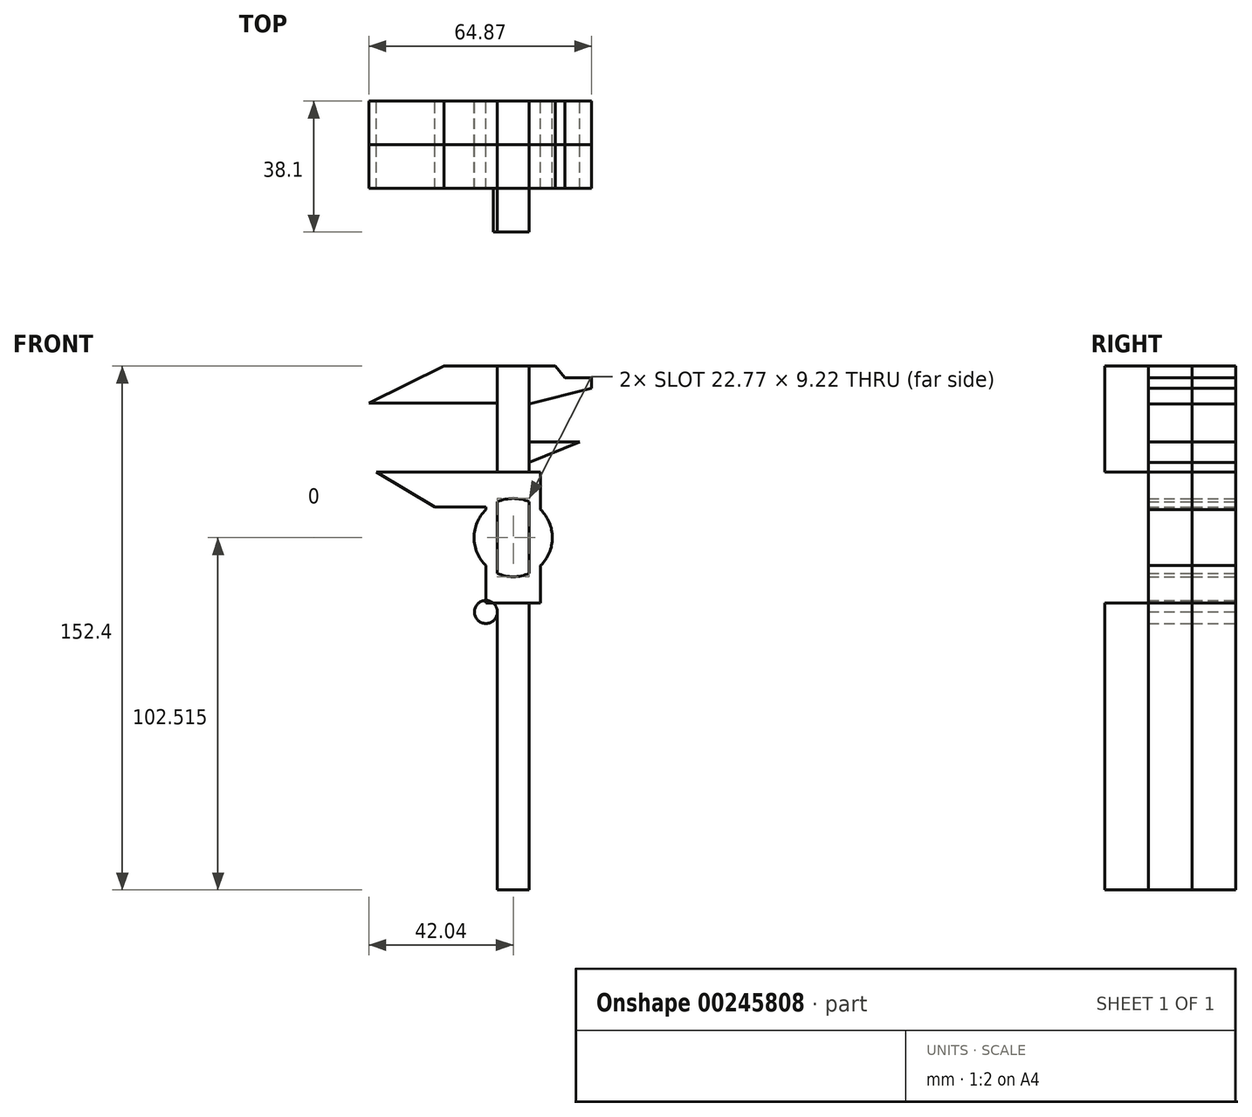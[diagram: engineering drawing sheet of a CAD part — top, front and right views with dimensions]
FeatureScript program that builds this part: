
annotation { "Feature Type Name" : "Feature", "Feature Type Description" : "" }
export const myFeature = defineFeature(function(context is Context, id is Id, definition is map)
    precondition{}
    {
        {
            var Q0;
            Q0=qCreatedBy(makeId("Front.planeOp"),FACE);
            var sketch = newSketch(context, id + "F0", { "sketchPlane" : qUnion([Q0])});
            skLineSegment(sketch, "E0.bottom", {"start": v(4.61, 76.2) * mm, "end": v(-4.61, 76.2) * mm});
            skLineSegment(sketch, "E0.top", {"start": v(4.61, -76.2) * mm, "end": v(-4.61, -76.2) * mm});
            skLineSegment(sketch, "E0.left", {"start": v(4.61, 76.2) * mm, "end": v(4.61, -76.2) * mm});
            skLineSegment(sketch, "E0.right", {"start": v(-4.61, 76.2) * mm, "end": v(-4.61, -76.2) * mm});
            skPoint(sketch, "E0.middle", {"position": v(0, 0) * mm});
            skLineSegment(sketch, "E1.bottom", {"start": v(7.97, 7.27) * mm, "end": v(-7.97, 7.27) * mm});
            skLineSegment(sketch, "E1.top", {"start": v(7.97, 45.37) * mm, "end": v(-7.97, 45.37) * mm});
            skLineSegment(sketch, "E1.left", {"start": v(7.97, 7.27) * mm, "end": v(7.97, 45.37) * mm});
            skLineSegment(sketch, "E1.right", {"start": v(-7.97, 7.27) * mm, "end": v(-7.97, 45.37) * mm});
            skPoint(sketch, "E1.middle", {"position": v(0, 26.32) * mm});
            skLineSegment(sketch, "E2", {"start": v(-4.61, 76.2) * mm, "end": v(-20.14, 76.2) * mm});
            skLineSegment(sketch, "E3", {"start": v(-20.14, 76.2) * mm, "end": v(-42.04, 65.5) * mm});
            skLineSegment(sketch, "E4", {"start": v(-42.04, 65.5) * mm, "end": v(-4.61, 65.5) * mm});
            skLineSegment(sketch, "E5", {"start": v(-7.97, 45.37) * mm, "end": v(-39.88, 45.37) * mm});
            skLineSegment(sketch, "E6", {"start": v(-39.88, 45.37) * mm, "end": v(-22.85, 35.24) * mm});
            skLineSegment(sketch, "E7", {"start": v(-22.85, 35.24) * mm, "end": v(-7.97, 35.24) * mm});
            skLineSegment(sketch, "E8", {"start": v(4.61, 76.2) * mm, "end": v(12.3, 76.2) * mm});
            skLineSegment(sketch, "E9", {"start": v(12.3, 76.2) * mm, "end": v(15, 72.8) * mm});
            skLineSegment(sketch, "E10", {"start": v(15, 72.8) * mm, "end": v(17.97, 72.8) * mm});
            skLineSegment(sketch, "E11", {"start": v(17.97, 72.8) * mm, "end": v(22.83, 72.8) * mm});
            skLineSegment(sketch, "E12", {"start": v(22.83, 72.8) * mm, "end": v(22.83, 69.83) * mm});
            skLineSegment(sketch, "E13", {"start": v(22.83, 69.83) * mm, "end": v(4.61, 65.24) * mm});
            skLineSegment(sketch, "E14", {"start": v(4.61, 54.16) * mm, "end": v(19.32, 54.16) * mm});
            skLineSegment(sketch, "E15", {"start": v(19.32, 54.16) * mm, "end": v(4.61, 48.2) * mm});
            skCircle(sketch, "E16", {"center": v(0, 26.32) * mm, "radius": 11.39 * mm});
            skCircle(sketch, "E17", {"center": v(-7.97, 4.7) * mm, "radius": 3.35 * mm});
            skSolve(sketch);
        }
        {
            var Q0;
            {var subQ0=sQuery(id+"F0.wireOp",EDGE,"E1.right");var subQ1=sQuery(id+"F0.wireOp",EDGE,"E1.bottom");var subQ2=makeQuery(id+"F0.imprint","INTERSECT",VERTEX,{"derivedFrom":[subQ1,subQ0]});Q0=makeQuery(id+"F0.imprint","IMPRINT",FACE,{"disambiguationData":[TD([[makeQuery(id+"F0.imprint","IMPRINT",EDGE,{"disambiguationData":[TD([[subQ2,1.0]])],"derivedFrom":subQ1}),-1.0]])]});}
            var Q1;
            {var subQ0=sQuery(id+"F0.wireOp",EDGE,"E17");var subQ1=sQuery(id+"F0.wireOp",EDGE,"E0.right");var subQ2=makeQuery(id+"F0.imprint","INTERSECT",VERTEX,{"derivedFrom":[subQ1,subQ0]});Q1=makeQuery(id+"F0.imprint","IMPRINT",FACE,{"disambiguationData":[TD([[makeQuery(id+"F0.imprint","IMPRINT",EDGE,{"disambiguationData":[TD([[subQ2,1.0]])],"derivedFrom":subQ1}),-1.0]])]});}
            var Q2;
            {var subQ5=sQuery(id+"F0.wireOp",EDGE,"E0.top");Q2=makeQuery(id+"F0.imprint","IMPRINT",FACE,{"disambiguationData":[TD([[makeQuery(id+"F0.imprint","IMPRINT",EDGE,{"derivedFrom":subQ5}),-1.0]])]});}
            var Q3;
            {var subQ5=sQuery(id+"F0.wireOp",EDGE,"E0.bottom");Q3=makeQuery(id+"F0.imprint","IMPRINT",FACE,{"disambiguationData":[TD([[makeQuery(id+"F0.imprint","IMPRINT",EDGE,{"derivedFrom":subQ5}),1.0]])]});}
            extrude(context, id + "F1", {"entities" : qUnion([Q0, Q1, Q2, Q3]), "depth" : 25.4 * mm});
        }
        {
            var Q0;
            Q0 = qSketchRegion(id + "F0", true);
            var Q1;
            Q1=makeQuery(id+"F1.opExtrude","CAP_FACE",FACE,{"disambiguationData":[OSD([sQuery(id+"F0.wireOp",EDGE,"E0.top"),sQuery(id+"F0.wireOp",EDGE,"E0.left"),sQuery(id+"F0.wireOp",EDGE,"E0.right"),sQuery(id+"F0.wireOp",EDGE,"E1.bottom"),sQuery(id+"F0.wireOp",EDGE,"E17")])],"isStart":false});
            var Q2;
            Q2=makeQuery(id+"F1.opExtrude","CAP_FACE",FACE,{"disambiguationData":[OSD([sQuery(id+"F0.wireOp",EDGE,"E0.bottom"),sQuery(id+"F0.wireOp",EDGE,"E0.left"),sQuery(id+"F0.wireOp",EDGE,"E0.right"),sQuery(id+"F0.wireOp",EDGE,"E1.top")])],"isStart":false});
            extrude(context, id + "F2", {"entities" : qUnion([Q0, Q1, Q2]), "depth" : 12.7 * mm});
        }
        {
            var Q0;
            Q0=makeQuery(id+"F2.opExtrude","CAP_FACE",FACE,{"disambiguationData":[OSD([sQuery(id+"F0.wireOp",EDGE,"E0.bottom"),sQuery(id+"F0.wireOp",EDGE,"E0.top"),sQuery(id+"F0.wireOp",EDGE,"E0.left"),sQuery(id+"F0.wireOp",EDGE,"E0.right"),sQuery(id+"F0.wireOp",EDGE,"E1.bottom"),sQuery(id+"F0.wireOp",EDGE,"E1.top"),sQuery(id+"F0.wireOp",EDGE,"E1.left"),sQuery(id+"F0.wireOp",EDGE,"E1.right"),sQuery(id+"F0.wireOp",EDGE,"E2"),sQuery(id+"F0.wireOp",EDGE,"E3"),sQuery(id+"F0.wireOp",EDGE,"E4"),sQuery(id+"F0.wireOp",EDGE,"E5"),sQuery(id+"F0.wireOp",EDGE,"E6"),sQuery(id+"F0.wireOp",EDGE,"E7"),sQuery(id+"F0.wireOp",EDGE,"E8"),sQuery(id+"F0.wireOp",EDGE,"E9"),sQuery(id+"F0.wireOp",EDGE,"E10"),sQuery(id+"F0.wireOp",EDGE,"E11"),sQuery(id+"F0.wireOp",EDGE,"E12"),sQuery(id+"F0.wireOp",EDGE,"E13"),sQuery(id+"F0.wireOp",EDGE,"E14"),sQuery(id+"F0.wireOp",EDGE,"E15"),sQuery(id+"F0.wireOp",EDGE,"E16"),sQuery(id+"F0.wireOp",EDGE,"E17")])],"isStart":false});
            extrude(context, id + "F3", {"entities" : qUnion([Q0]), "depth" : 12.7 * mm});
        }
    });
